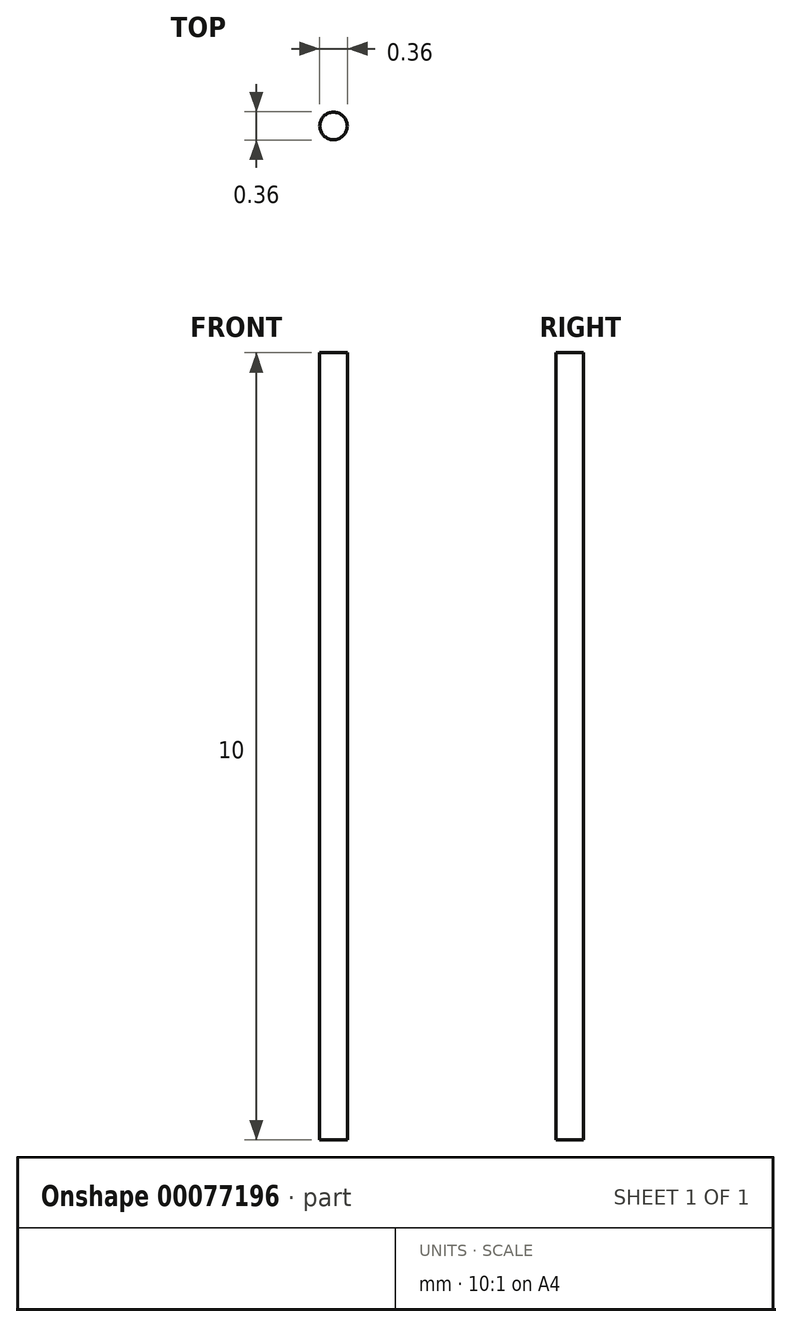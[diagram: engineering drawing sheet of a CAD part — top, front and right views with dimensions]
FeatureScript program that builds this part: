
annotation { "Feature Type Name" : "Feature", "Feature Type Description" : "" }
export const myFeature = defineFeature(function(context is Context, id is Id, definition is map)
    precondition{}
    {
        {
            var Q0;
            Q0=qCreatedBy(makeId("Top.planeOp"),FACE);
            var sketch = newSketch(context, id + "F0", { "sketchPlane" : qUnion([Q0])});
            skCircle(sketch, "E0", {"center": v(0, 0) * mm, "radius": 0.18 * mm});
            skSolve(sketch);
        }
        {
            var Q0;
            Q0=qSketchRegion(id+"F0",true);
            extrude(context, id + "F1", {"entities" : qUnion([Q0]), "depth" : 10 * mm});
        }
    });
